# Revit family: Faucet-Two_Handle-American_Standard-Serin-2064.831
name_source: partatom
category: Plumbing Fixtures
revit_build: Autodesk Revit 2014 (Build: 20130308_1515(x64)
units: mm (PartAtom-declared; Revit-internal decimal feet)

## types (1)
- 2064.831
    ADA Compliant = Yes
    Assembly Code = D2020300
    CW Connection = Yes
    CWFU = 1.5
    Cold Water Connection Diameter = 1/2"
    Default Elevation = 0"
    Description = Serin Two-Handle Widespread Lavatory Faucet With Brass Spout
    Finish = Brass-American Standard-002-Polished Chrome
    Flow Rate = 1 GPM
    HW Connection = Yes
    HWFU = 1.5
    Height = 9 5/8"
    Hot Water Connection Diameter = 1/2"
    Installation Type = Deck Mounted
    Length = 8"
    Manufacturer = American Standard
    Material = Brass-American Standard-002-Polished Chrome
    Model = 2064.831
    Price = Prices may vary. Please consult Manufacturer Representative for most up-to-date price list.
    Product Documentation Link = https://www.americanstandard-us.com
    Product Page URL = https://www.americanstandard-us.com
    Revised Date = 12/06/2017
    Specification = Two-handle widespread lavatory faucet shall feature cast brass valve bodies with flexible hose connections for 6in to 12in installations. Shall also feature 1/4 turn washerless ceramic disc valve cartridges. Shall also feature a metal drain body with stainless steel cable actuation.
    URL = http://www.americanstandard-us.com
    Vent Connection = No
    WFU = 2
    Warranty Information = Limited Lifetime Function and Finish Warranty
    Waste Connection = Yes
    Width = 2 1/16"

## geometry (parser evidence)
native form markers: Sweep x1
no freeform markers — native parametric forms only
